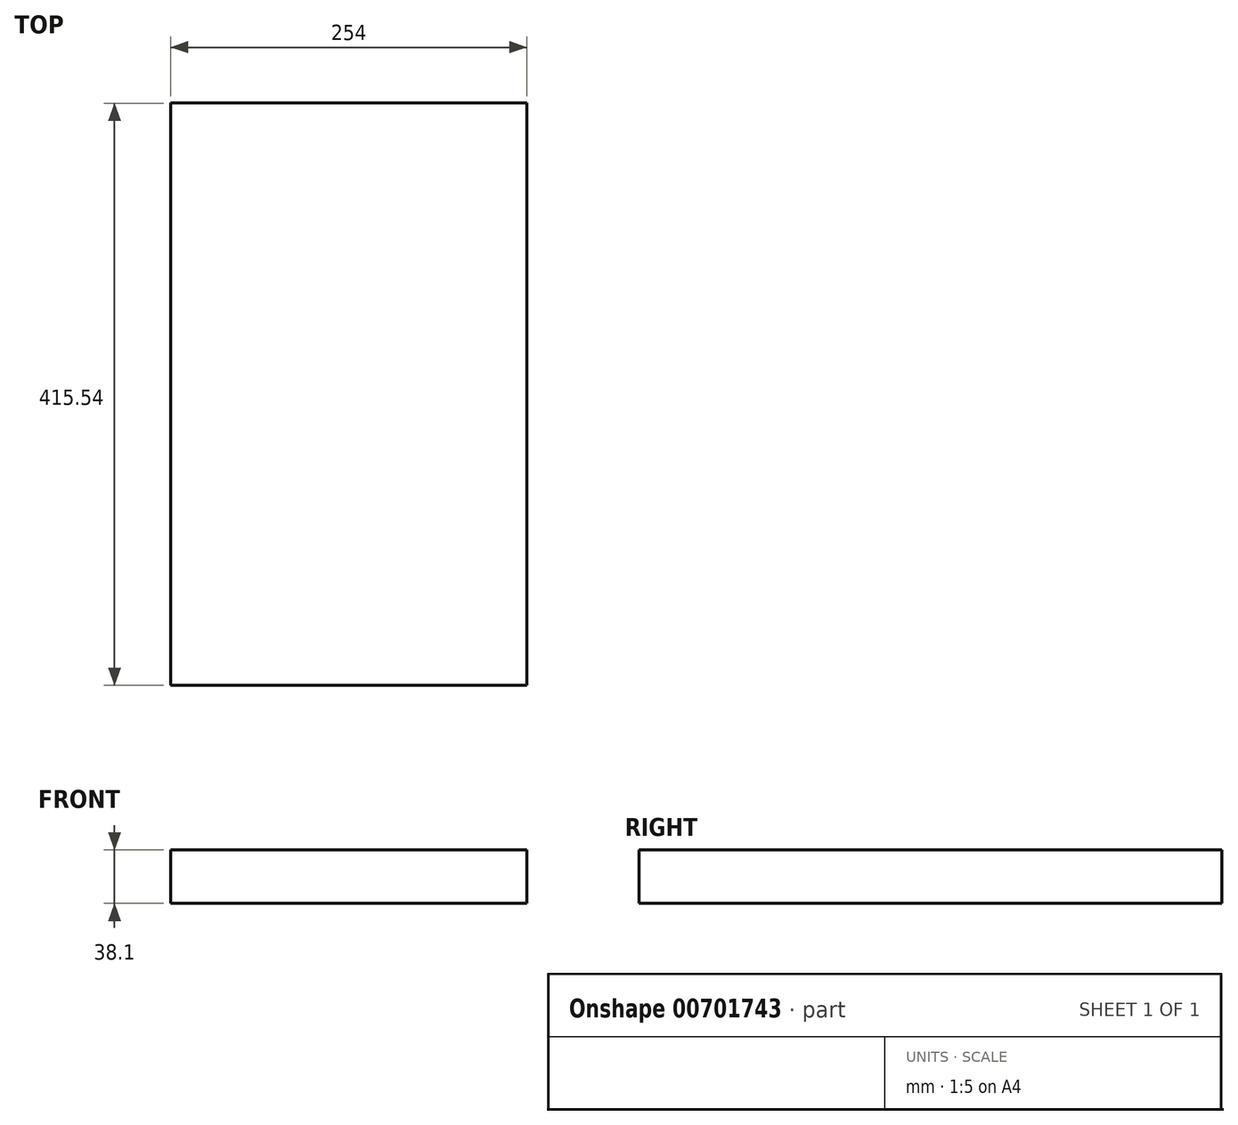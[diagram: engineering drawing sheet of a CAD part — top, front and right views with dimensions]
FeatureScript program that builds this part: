
annotation { "Feature Type Name" : "Feature", "Feature Type Description" : "" }
export const myFeature = defineFeature(function(context is Context, id is Id, definition is map)
    precondition{}
    {
        {
            var Q0;
            Q0=qCreatedBy(makeId("Front.planeOp"),FACE);
            var sketch = newSketch(context, id + "F0", { "sketchPlane" : qUnion([Q0])});
            skLineSegment(sketch, "E0.bottom", {"start": v(-138.11, -14.67) * mm, "end": v(115.89, -14.67) * mm});
            skLineSegment(sketch, "E0.top", {"start": v(-138.11, -52.77) * mm, "end": v(115.89, -52.77) * mm});
            skLineSegment(sketch, "E0.left", {"start": v(-138.11, -14.67) * mm, "end": v(-138.11, -52.77) * mm});
            skLineSegment(sketch, "E0.right", {"start": v(115.89, -14.67) * mm, "end": v(115.89, -52.77) * mm});
            skLineSegment(sketch, "E1.bottom", {"start": v(12.03, 86.93) * mm, "end": v(115.89, 86.93) * mm});
            skLineSegment(sketch, "E1.top", {"start": v(12.03, -14.67) * mm, "end": v(115.89, -14.67) * mm});
            skLineSegment(sketch, "E1.left", {"start": v(12.03, 86.93) * mm, "end": v(12.03, -14.67) * mm});
            skLineSegment(sketch, "E1.right", {"start": v(115.89, 86.93) * mm, "end": v(115.89, -14.67) * mm});
            skLineSegment(sketch, "E2.bottom", {"start": v(115.89, 86.93) * mm, "end": v(185.79, 86.93) * mm});
            skLineSegment(sketch, "E2.top", {"start": v(115.89, 39.17) * mm, "end": v(185.79, 39.17) * mm});
            skLineSegment(sketch, "E2.left", {"start": v(115.89, 86.93) * mm, "end": v(115.89, 39.17) * mm});
            skLineSegment(sketch, "E2.right", {"start": v(185.79, 86.93) * mm, "end": v(185.79, 39.17) * mm});
            skSolve(sketch);
        }
        {
            var Q0;
            Q0=makeQuery(id+"F0.imprint","IMPRINT",FACE,{"disambiguationData":[TD([[makeQuery(id+"F0.imprint","IMPRINT",EDGE,{"derivedFrom":sQuery(id+"F0.wireOp",EDGE,"E0.bottom")}),-1.0]])]});
            extrude(context, id + "F1", {"entities" : qUnion([Q0]), "endBound" : BoundingType.SYMMETRIC, "depth" : 415.54 * mm, "offsetDistance" : 25.4 * mm});
        }
    });
